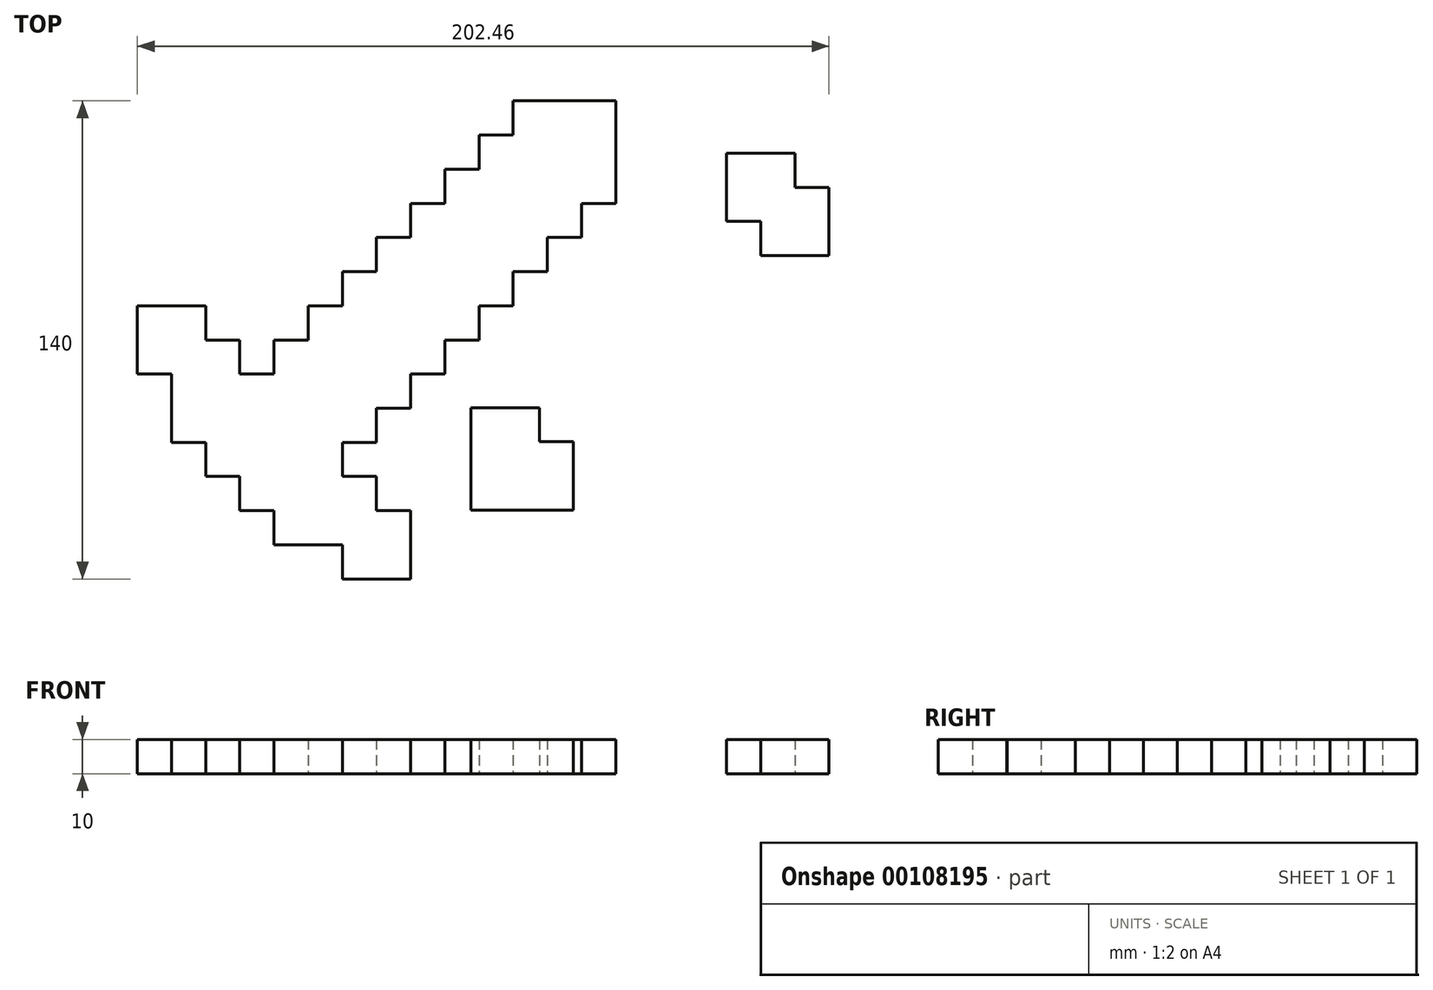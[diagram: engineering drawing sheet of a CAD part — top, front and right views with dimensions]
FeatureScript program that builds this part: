
annotation { "Feature Type Name" : "Feature", "Feature Type Description" : "" }
export const myFeature = defineFeature(function(context is Context, id is Id, definition is map)
    precondition{}
    {
        {
            var Q0;
            Q0=qCreatedBy(makeId("Top.planeOp"), FACE);
            var sketch = newSketch(context, id + "F0", { "sketchPlane" : qUnion([Q0])});
            skLineSegment(sketch, "E0", {"start": v(0, 15.3) * mm, "end": v(-30, 15.3) * mm});
            skLineSegment(sketch, "E1", {"start": v(-30, 15.3) * mm, "end": v(-30, 5.3) * mm});
            skLineSegment(sketch, "E2", {"start": v(-30, 5.3) * mm, "end": v(-40, 5.3) * mm});
            skLineSegment(sketch, "E3", {"start": v(-40, 5.3) * mm, "end": v(-40, -4.7) * mm});
            skLineSegment(sketch, "E4", {"start": v(-40, -4.7) * mm, "end": v(-50, -4.7) * mm});
            skLineSegment(sketch, "E5", {"start": v(-50, -4.7) * mm, "end": v(-50, -14.7) * mm});
            skLineSegment(sketch, "E6", {"start": v(-50, -14.7) * mm, "end": v(-60, -14.7) * mm});
            skLineSegment(sketch, "E7", {"start": v(-60, -14.7) * mm, "end": v(-60, -24.7) * mm});
            skLineSegment(sketch, "E8", {"start": v(-60, -24.7) * mm, "end": v(-70, -24.7) * mm});
            skLineSegment(sketch, "E9", {"start": v(-70, -24.7) * mm, "end": v(-70, -34.7) * mm});
            skLineSegment(sketch, "E10", {"start": v(-70, -34.7) * mm, "end": v(-80, -34.7) * mm});
            skLineSegment(sketch, "E11", {"start": v(-80, -34.7) * mm, "end": v(-80, -44.7) * mm});
            skLineSegment(sketch, "E12", {"start": v(-80, -44.7) * mm, "end": v(-90, -44.7) * mm});
            skLineSegment(sketch, "E13", {"start": v(-90, -44.7) * mm, "end": v(-90, -54.7) * mm});
            skLineSegment(sketch, "E14", {"start": v(-90, -54.7) * mm, "end": v(-100, -54.7) * mm});
            skLineSegment(sketch, "E15", {"start": v(-100, -54.7) * mm, "end": v(-100, -64.7) * mm});
            skLineSegment(sketch, "E16", {"start": v(-100, -64.7) * mm, "end": v(-110, -64.7) * mm});
            skLineSegment(sketch, "E17", {"start": v(-110, -64.7) * mm, "end": v(-110, -54.7) * mm});
            skLineSegment(sketch, "E18", {"start": v(-110, -54.7) * mm, "end": v(-120, -54.7) * mm});
            skLineSegment(sketch, "E19", {"start": v(-120, -54.7) * mm, "end": v(-120, -44.7) * mm});
            skLineSegment(sketch, "E20", {"start": v(-120, -44.7) * mm, "end": v(-140, -44.7) * mm});
            skLineSegment(sketch, "E21", {"start": v(-140, -44.7) * mm, "end": v(-140, -64.7) * mm});
            skLineSegment(sketch, "E22", {"start": v(-140, -64.7) * mm, "end": v(-130, -64.7) * mm});
            skLineSegment(sketch, "E23", {"start": v(-130, -64.7) * mm, "end": v(-130, -84.7) * mm});
            skLineSegment(sketch, "E24", {"start": v(-130, -84.7) * mm, "end": v(-120, -84.7) * mm});
            skLineSegment(sketch, "E25", {"start": v(-120, -84.7) * mm, "end": v(-120, -94.7) * mm});
            skLineSegment(sketch, "E26", {"start": v(-120, -94.7) * mm, "end": v(-110, -94.7) * mm});
            skLineSegment(sketch, "E27", {"start": v(0, 15.3) * mm, "end": v(-110, -94.7) * mm, "construction": true});
            skLineSegment(sketch, "E28.MirrorCS", {"start": v(0, 15.3) * mm, "end": v(0, -14.7) * mm});
            skLineSegment(sketch, "E29.MirrorCS", {"start": v(0, -14.7) * mm, "end": v(-10, -14.7) * mm});
            skLineSegment(sketch, "E30.MirrorCS", {"start": v(-10, -14.7) * mm, "end": v(-10, -24.7) * mm});
            skLineSegment(sketch, "E31.MirrorCS", {"start": v(-10, -24.7) * mm, "end": v(-20, -24.7) * mm});
            skLineSegment(sketch, "E32.MirrorCS", {"start": v(-20, -24.7) * mm, "end": v(-20, -34.7) * mm});
            skLineSegment(sketch, "E33.MirrorCS", {"start": v(-20, -34.7) * mm, "end": v(-30, -34.7) * mm});
            skLineSegment(sketch, "E34.MirrorCS", {"start": v(-30, -34.7) * mm, "end": v(-30, -44.7) * mm});
            skLineSegment(sketch, "E35.MirrorCS", {"start": v(-30, -44.7) * mm, "end": v(-40, -44.7) * mm});
            skLineSegment(sketch, "E36.MirrorCS", {"start": v(-40, -44.7) * mm, "end": v(-40, -54.7) * mm});
            skLineSegment(sketch, "E37.MirrorCS", {"start": v(-40, -54.7) * mm, "end": v(-50, -54.7) * mm});
            skLineSegment(sketch, "E38.MirrorCS", {"start": v(-50, -54.7) * mm, "end": v(-50, -64.7) * mm});
            skLineSegment(sketch, "E39.MirrorCS", {"start": v(-50, -64.7) * mm, "end": v(-60, -64.7) * mm});
            skLineSegment(sketch, "E40.MirrorCS", {"start": v(-60, -64.7) * mm, "end": v(-60, -74.7) * mm});
            skLineSegment(sketch, "E41.MirrorCS", {"start": v(-60, -74.7) * mm, "end": v(-70, -74.7) * mm});
            skLineSegment(sketch, "E42.MirrorCS", {"start": v(-70, -74.7) * mm, "end": v(-70, -84.7) * mm});
            skLineSegment(sketch, "E43.MirrorCS", {"start": v(-70, -84.7) * mm, "end": v(-80, -84.7) * mm});
            skLineSegment(sketch, "E44.MirrorCS", {"start": v(-80, -84.7) * mm, "end": v(-80, -94.7) * mm});
            skLineSegment(sketch, "E45.MirrorCS", {"start": v(-80, -94.7) * mm, "end": v(-70, -94.7) * mm});
            skLineSegment(sketch, "E46.MirrorCS", {"start": v(-70, -94.7) * mm, "end": v(-70, -104.7) * mm});
            skLineSegment(sketch, "E47.MirrorCS", {"start": v(-70, -104.7) * mm, "end": v(-60, -104.7) * mm});
            skLineSegment(sketch, "E48.MirrorCS", {"start": v(-60, -104.7) * mm, "end": v(-60, -124.7) * mm});
            skLineSegment(sketch, "E49.MirrorCS", {"start": v(-60, -124.7) * mm, "end": v(-80, -124.7) * mm});
            skLineSegment(sketch, "E50.MirrorCS", {"start": v(-80, -124.7) * mm, "end": v(-80, -114.7) * mm});
            skLineSegment(sketch, "E51.MirrorCS", {"start": v(-80, -114.7) * mm, "end": v(-100, -114.7) * mm});
            skLineSegment(sketch, "E52.MirrorCS", {"start": v(-100, -114.7) * mm, "end": v(-100, -104.7) * mm});
            skLineSegment(sketch, "E53.MirrorCS", {"start": v(-100, -104.7) * mm, "end": v(-110, -104.7) * mm});
            skLineSegment(sketch, "E54.MirrorCS", {"start": v(-110, -104.7) * mm, "end": v(-110, -94.7) * mm});
            skLineSegment(sketch, "E55", {"start": v(-42.32, -74.53) * mm, "end": v(-22.32, -74.53) * mm});
            skLineSegment(sketch, "E56", {"start": v(-22.32, -74.53) * mm, "end": v(-22.32, -84.53) * mm});
            skLineSegment(sketch, "E57", {"start": v(-22.32, -84.53) * mm, "end": v(-12.32, -84.53) * mm});
            skLineSegment(sketch, "E58", {"start": v(-12.32, -84.53) * mm, "end": v(-12.32, -104.53) * mm});
            skLineSegment(sketch, "E59", {"start": v(-12.32, -104.53) * mm, "end": v(-42.32, -104.53) * mm});
            skLineSegment(sketch, "E60", {"start": v(-42.32, -104.53) * mm, "end": v(-42.32, -74.53) * mm});
            skLineSegment(sketch, "E61", {"start": v(32.46, 0) * mm, "end": v(32.46, -20) * mm});
            skLineSegment(sketch, "E62", {"start": v(32.46, -20) * mm, "end": v(42.46, -20) * mm});
            skLineSegment(sketch, "E63", {"start": v(42.46, -20) * mm, "end": v(42.46, -30) * mm});
            skLineSegment(sketch, "E64", {"start": v(42.46, -30) * mm, "end": v(62.46, -30) * mm});
            skLineSegment(sketch, "E65", {"start": v(62.46, -30) * mm, "end": v(62.46, -10) * mm});
            skLineSegment(sketch, "E66", {"start": v(62.46, -10) * mm, "end": v(52.46, -10) * mm});
            skLineSegment(sketch, "E67", {"start": v(52.46, -10) * mm, "end": v(52.46, 0) * mm});
            skLineSegment(sketch, "E68", {"start": v(52.46, 0) * mm, "end": v(32.46, 0) * mm});
            skSolve(sketch);
        }
        {
            var Q0;
            Q0 = qSketchRegion(id + "F0", true);
            extrude(context, id + "F1", {"entities" : qUnion([Q0]), "depth" : 10 * mm, "offsetDistance" : 25 * mm});
        }
    });
